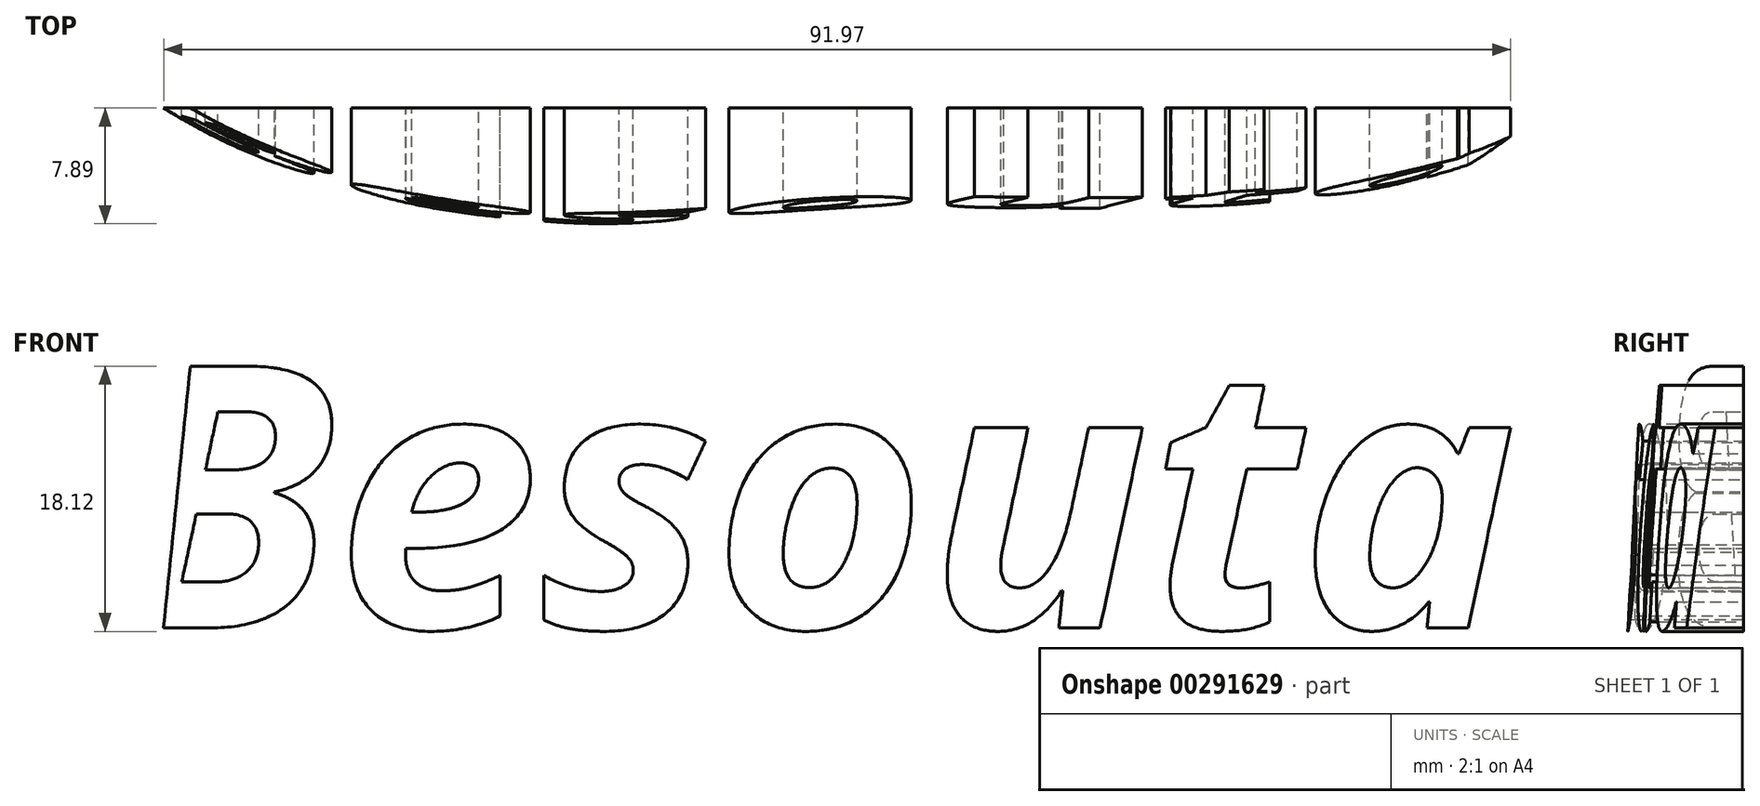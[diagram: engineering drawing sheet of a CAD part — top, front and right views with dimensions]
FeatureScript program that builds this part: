
annotation { "Feature Type Name" : "Feature", "Feature Type Description" : "" }
export const myFeature = defineFeature(function(context is Context, id is Id, definition is map)
    precondition{}
    {
        {
            var Q0;
            Q0=qCreatedBy(makeId("Front.planeOp"),FACE);
            var sketch = newSketch(context, id + "F0", { "sketchPlane" : qUnion([Q0])});
            skArc(sketch, "E0", {"start": v(35.3, 14.31) * mm, "mid": v(-38.1, 0) * mm, "end": v(35.3, -14.31) * mm});
            skPoint(sketch, "E1.end.orphan", {"position": v(13.77, 0) * mm});
            skPoint(sketch, "E2.start.orphan", {"position": v(0, 2.75) * mm});
            skLineSegment(sketch, "E3", {"start": v(0, 0) * mm, "end": v(35.3, 14.31) * mm});
            skLineSegment(sketch, "E4", {"start": v(0, 0) * mm, "end": v(35.3, -14.31) * mm});
            skCircle(sketch, "E5", {"center": v(4.82, 18.94) * mm, "radius": 6.35 * mm});
            skSolve(sketch);
        }
        {
            var Q0;
            Q0=makeQuery(id+"F0.imprint","IMPRINT",FACE,{"disambiguationData":[TD([[makeQuery(id+"F0.imprint","IMPRINT",EDGE,{"derivedFrom":sQuery(id+"F0.wireOp",EDGE,"E0")}),1.0]])]});
            extrude(context, id + "F1", {"entities" : qUnion([Q0]), "endBound" : BoundingType.SYMMETRIC, "depth" : 38.1 * mm});
        }
        {
            var Q0;
            Q0=makeQuery(id+"F1.opExtrude","CAP_FACE",FACE,{"disambiguationData":[OSD([sQuery(id+"F0.wireOp",EDGE,"E0"),sQuery(id+"F0.wireOp",EDGE,"E3"),sQuery(id+"F0.wireOp",EDGE,"E4"),sQuery(id+"F0.wireOp",EDGE,"E5")])],"isStart":false});
            var Q1;
            Q1=makeQuery(id+"F1.opExtrude","SWEPT_FACE",FACE,{"disambiguationData":[OSD([sQuery(id+"F0.wireOp",EDGE,"E0")])]});
            fillet(context, id + "F2", {"entities" : qUnion([Q0, Q1]), "radius" : 5.08 * mm, "tangentPropagation" : true, "allowEdgeOverflow" : false});
        }
        {
            var Q0;
            Q0=makeQuery(id+"F1.opExtrude","CAP_FACE",FACE,{"disambiguationData":[OSD([sQuery(id+"F0.wireOp",EDGE,"E0"),sQuery(id+"F0.wireOp",EDGE,"E3"),sQuery(id+"F0.wireOp",EDGE,"E4"),sQuery(id+"F0.wireOp",EDGE,"E5")])],"isStart":true});
            fillet(context, id + "F3", {"entities" : qUnion([Q0]), "radius" : 5.08 * mm, "tangentPropagation" : true, "allowEdgeOverflow" : false});
        }
        {
            var Q0;
            Q0=qCreatedBy(makeId("Top.planeOp"),FACE);
            var sketch = newSketch(context, id + "F4", { "sketchPlane" : qUnion([Q0])});
            skFitSpline(sketch, "E6", {"points": [v(0, -33.03) * mm, v(-19.96, -34.12) * mm, v(-54.44, -20.32) * mm, v(-55.9, 26.13) * mm, v(41.37, 31.58) * mm, v(55.53, 0) * mm, v(45, -27.95) * mm, v(0, -33.03) * mm]});
            skSolve(sketch);
        }
        {
            var Q0;
            Q0=makeQuery(id+"F4.imprint","IMPRINT",FACE,{"disambiguationData":[TD([[makeQuery(id+"F4.imprint","IMPRINT",EDGE,{"derivedFrom":sQuery(id+"F4.wireOp",EDGE,"E6")}),-1.0]])]});
            extrude(context, id + "F5", {"entities" : qUnion([Q0]), "oppositeDirection" : true, "depth" : 76.2 * mm, "hasDraft" : true, "draftAngle" : 3 * degree});
        }
        {
            var Q0;
            Q0=makeQuery(id+"F5.opExtrude","CAP_FACE",FACE,{"disambiguationData":[OSD([sQuery(id+"F4.wireOp",EDGE,"E6")])],"isStart":false});
            var Q1;
            Q1=makeQuery(id+"F5.opExtrude","SWEPT_FACE",FACE,{"disambiguationData":[OSD([sQuery(id+"F4.wireOp",EDGE,"E6")])]});
            fillet(context, id + "F6", {"entities" : qUnion([Q0, Q1]), "radius" : 2.54 * mm, "tangentPropagation" : true, "allowEdgeOverflow" : false});
        }
        {
            var Q0;
            Q0=qCreatedBy(makeId("Front.planeOp"),FACE);
            cPlane(context, id + "F7", {"entities" : qUnion([Q0]), "cplaneType" : CPlaneType.OFFSET, "offset" : 41.66 * mm, "width" : 152.4 * mm, "height" : 152.4 * mm});
        }
        {
            var Q0;
            Q0=qCreatedBy(id+"F7.planeOp",FACE);
            var sketch = newSketch(context, id + "F8", { "sketchPlane" : qUnion([Q0])});
            skText(sketch, "E7", { "text": "Besouta", "fontName": "OpenSans-BoldItalic.ttf"});
            const initialGuessF8  = {"E7": [-0.05203, -0.05138, 1, 0, 0.01802]};
            skSetInitialGuess(sketch, initialGuessF8);
            skSolve(sketch);
        }
        {
            var Q0;
            Q0 = qSketchRegion(id + "F8", true);
            extrude(context, id + "F9", {"entities" : qUnion([Q0]), "operationType" : NewBodyOperationType.INTERSECT, "endBound" : BoundingType.SYMMETRIC, "depth" : 25.4 * mm});
        }
    });
